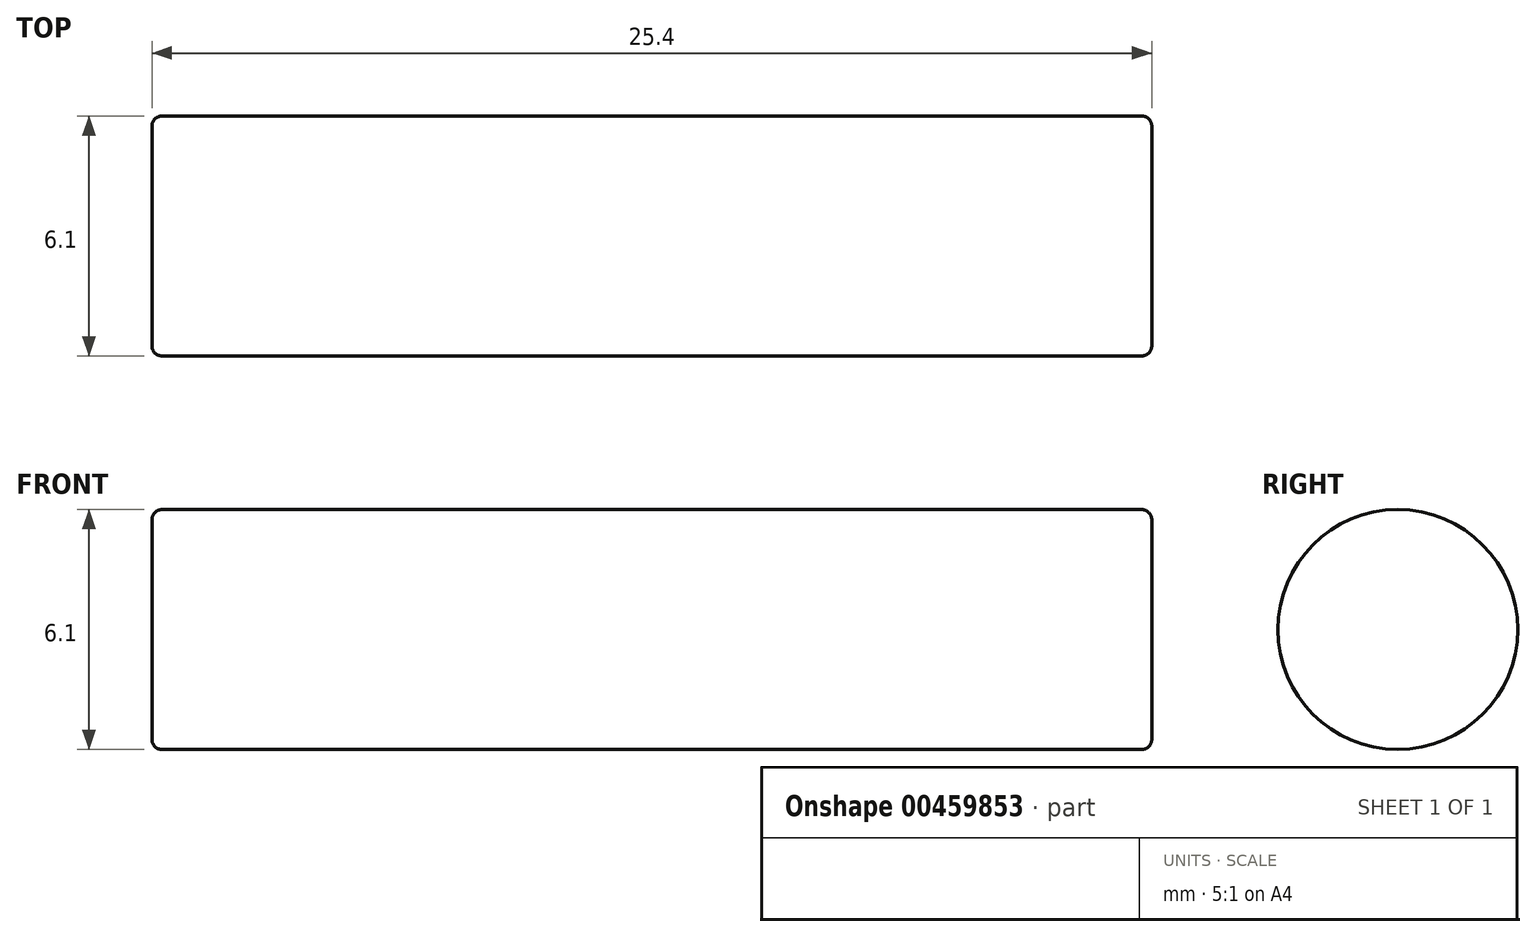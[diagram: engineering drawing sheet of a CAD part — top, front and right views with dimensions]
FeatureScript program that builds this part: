
annotation { "Feature Type Name" : "Feature", "Feature Type Description" : "" }
export const myFeature = defineFeature(function(context is Context, id is Id, definition is map)
    precondition{}
    {
        {
            var Q0;
            Q0=qCreatedBy(makeId("Right.planeOp"),FACE);
            var sketch = newSketch(context, id + "F0", { "sketchPlane" : qUnion([Q0])});
            skCircle(sketch, "E0", {"center": v(0, 0) * mm, "radius": 3.05 * mm});
            skSolve(sketch);
        }
        {
            var Q0;
            Q0 = qSketchRegion(id + "F0", true);
            extrude(context, id + "F1", {"entities" : qUnion([Q0]), "depth" : 25.4 * mm});
        }
        {
            var Q0;
            Q0=makeQuery(id+"F1.opExtrude","CAP_FACE",FACE,{"disambiguationData":[OSD([sQuery(id+"F0.wireOp",EDGE,"E0")])],"isStart":false});
            var Q1;
            Q1=makeQuery(id+"F1.opExtrude","CAP_FACE",FACE,{"disambiguationData":[OSD([sQuery(id+"F0.wireOp",EDGE,"E0")])],"isStart":true});
            fillet(context, id + "F2", {"entities" : qUnion([Q0, Q1]), "radius" : 0.25 * mm, "tangentPropagation" : true, "allowEdgeOverflow" : false});
        }
    });
